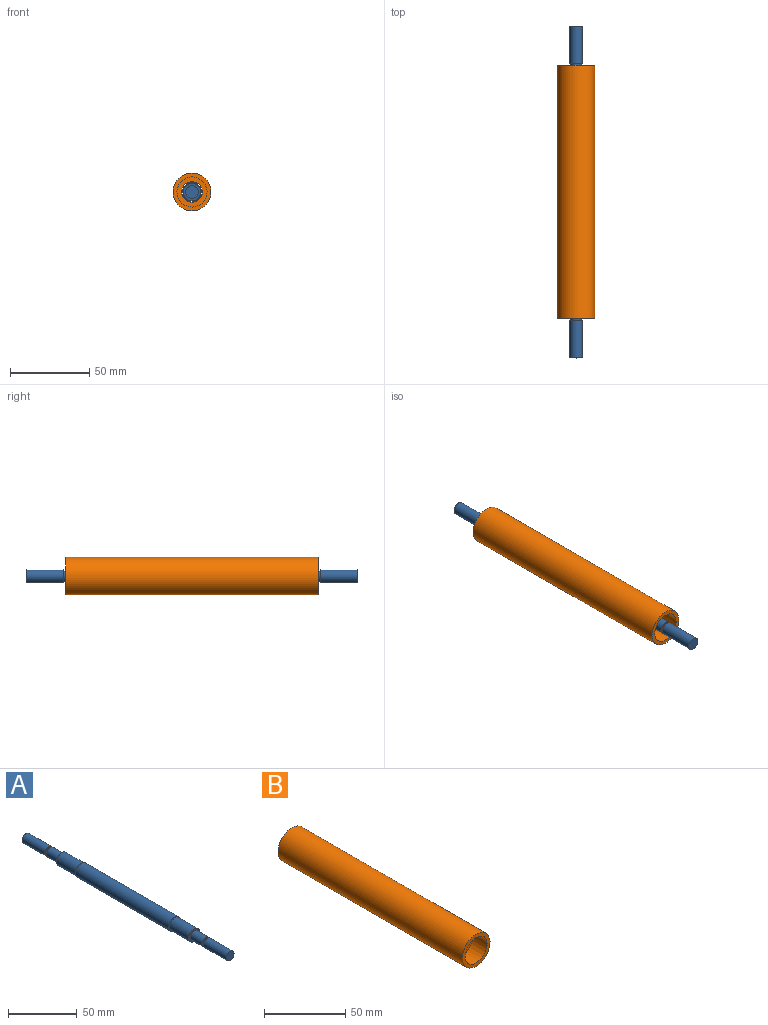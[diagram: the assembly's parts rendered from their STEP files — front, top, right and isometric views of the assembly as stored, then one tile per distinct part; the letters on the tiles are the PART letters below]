
ASSEMBLY  parts=2 mates=1
PART A: 19 faces, bbox 12x210x12 mm
  f0: plane 12x12mm, normal (0,-1,0), area 18.1mm2, adj f1,f18
  f1: cylinder r=5.5mm len=20mm, axis (0,-1,0), area 691.2mm2, adj f0,f2
  f2: plane 11x11mm, normal (0,-1,0), area 44.8mm2, adj f1,f3
  f3: cylinder r=4mm len=12mm, axis (0,-1,0), area 301.6mm2, adj f2,f4
  f4: plane 8x8mm, normal (0,-1,0), area 17.1mm2, adj f3,f5
  f5: cylinder r=3.25mm len=6.5mm, axis (0,-1,0), area 30.6mm2, adj f4,f6
  f6: plane 8x8mm, normal (0,1,0), area 17.1mm2, adj f5,f7
  f7: cylinder r=4mm len=23.5mm, axis (0,-1,0), area 590.6mm2, adj f6,f8
  f8: plane 8x8mm, normal (0,-1,0), area 50.3mm2, adj f7
  f9: plane 8x8mm, normal (0,1,0), area 50.3mm2, adj f10
  f10: cylinder r=4mm len=23.5mm, axis (0,-1,0), area 590.6mm2, adj f9,f11
  f11: plane 8x8mm, normal (0,-1,0), area 17.1mm2, adj f10,f12
  f12: cylinder r=3.25mm len=6.5mm, axis (0,-1,0), area 30.6mm2, adj f11,f13
  f13: plane 8x8mm, normal (0,1,0), area 17.1mm2, adj f12,f14
  f14: cylinder r=4mm len=12mm, axis (0,-1,0), area 301.6mm2, adj f13,f15
  f15: plane 11x11mm, normal (0,1,0), area 44.8mm2, adj f14,f16
  f16: cylinder r=5.5mm len=20mm, axis (0,-1,0), area 691.2mm2, adj f15,f17
  f17: plane 12x12mm, normal (0,1,0), area 18.1mm2, adj f16,f18
  f18: cylinder r=6mm len=96mm, axis (0,-1,0), area 3619.1mm2, adj f0,f17
PART B: 8 faces, bbox 24x160x24 mm
  f0: cylinder r=6.5mm len=135mm, axis (0,1,0), area 5513.5mm2, adj f5,f7
  f1: cylinder r=12mm len=160mm, axis (0,1,0), area 12063.7mm2, adj f2,f3
  f2: plane 24x24mm, normal (0,-1,0), area 168.9mm2, adj f1,f4
  f3: plane 24x24mm, normal (0,1,0), area 168.9mm2, adj f1,f6
  f4: cone r=9.5mm half-angle=3deg, axis (0,1,0), area 772.9mm2, adj f2,f5
  f5: plane 20.31x20.31mm, normal (0,-1,0), area 191.2mm2, adj f0,f4
  f6: cylinder r=9.5mm len=19mm, axis (0,1,0), area 746.1mm2, adj f3,f7
  f7: plane 19x19mm, normal (0,1,0), area 150.8mm2, adj f0,f6
PLACE A t=(-25.32,-73.93,-101.98)mm
PLACE B t=(-25.32,111.07,-101.98)mm
MATE fastened A.f1 <-> B.f4  axis (0,-1,0) through (-25.32,-48.93,-101.98)mm
